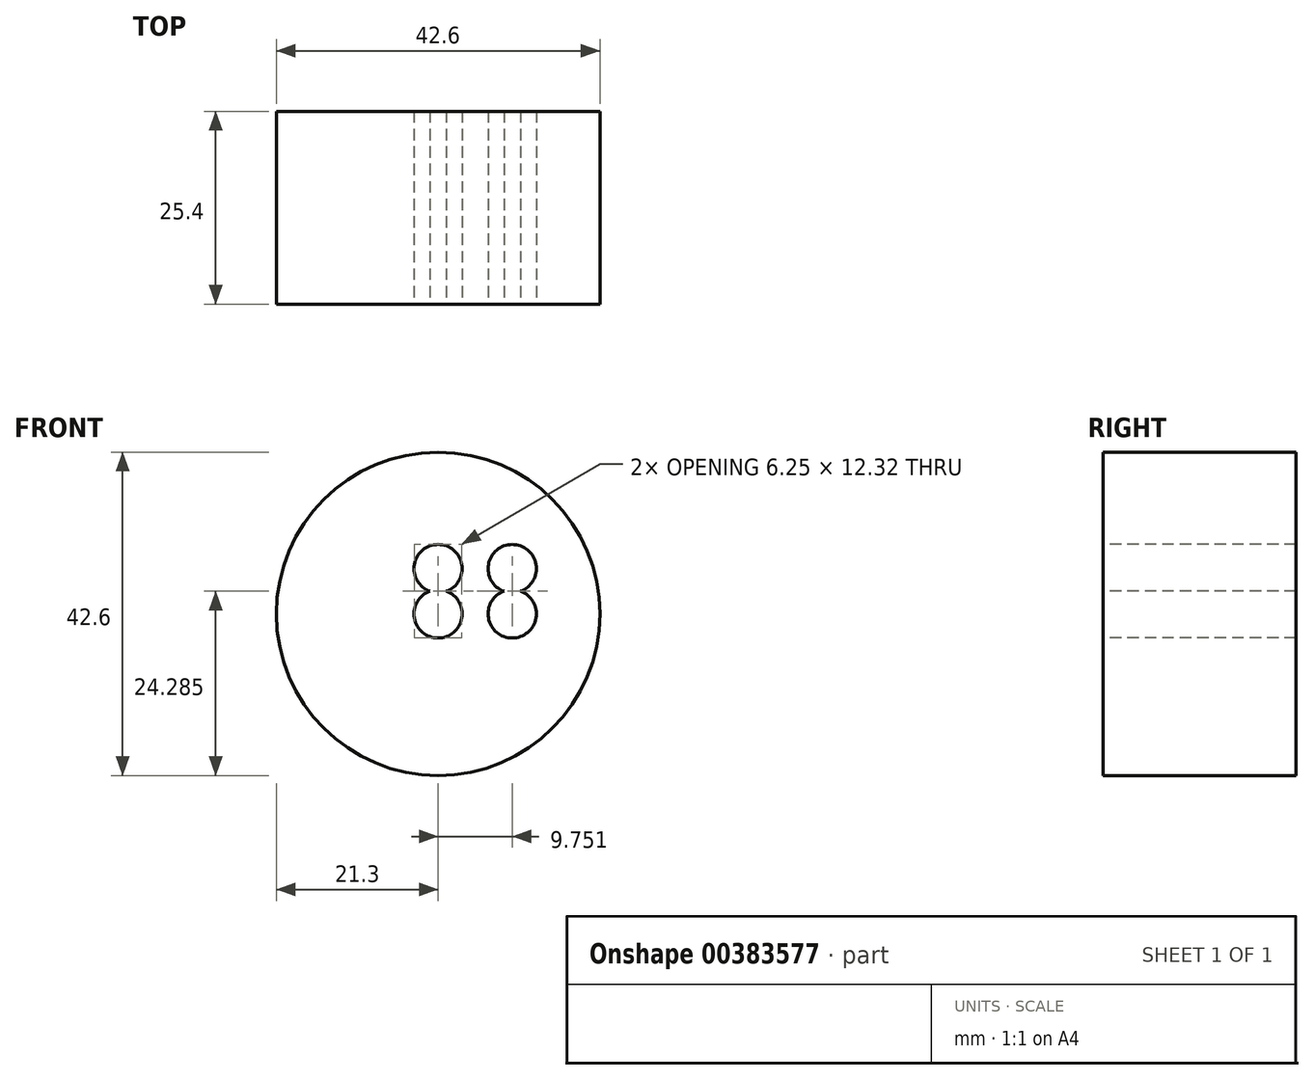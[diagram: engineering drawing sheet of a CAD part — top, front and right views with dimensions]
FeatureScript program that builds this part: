
annotation { "Feature Type Name" : "Feature", "Feature Type Description" : "" }
export const myFeature = defineFeature(function(context is Context, id is Id, definition is map)
    precondition{}
    {
        {
            var Q0;
            Q0=qCreatedBy(makeId("Front.planeOp"),FACE);
            var sketch = newSketch(context, id + "F0", { "sketchPlane" : qUnion([Q0])});
            skCircle(sketch, "E0", {"center": v(0, 0) * mm, "radius": 21.3 * mm});
            skSolve(sketch);
        }
        {
            var Q0;
            Q0 = qSketchRegion(id + "F0", true);
            extrude(context, id + "F1", {"entities" : qUnion([Q0]), "oppositeDirection" : true, "depth" : 25.4 * mm});
        }
        {
            var Q0;
            Q0=qCreatedBy(makeId("Front.planeOp"),FACE);
            var sketch = newSketch(context, id + "F2", { "sketchPlane" : qUnion([Q0])});
            skLineSegment(sketch, "E1.bottom", {"start": v(0, 0) * mm, "end": v(9.75, 0) * mm});
            skLineSegment(sketch, "E1.top", {"start": v(0, 5.97) * mm, "end": v(9.75, 5.97) * mm});
            skLineSegment(sketch, "E1.left", {"start": v(0, 0) * mm, "end": v(0, 5.97) * mm});
            skLineSegment(sketch, "E1.right", {"start": v(9.75, 0) * mm, "end": v(9.75, 5.97) * mm});
            skSolve(sketch);
        }
        {
            var Q0;
            Q0=sQuery(id+"F2.wireOp",VERTEX,"E1.right.start");
            var Q1;
            Q1=sQuery(id+"F2.wireOp",VERTEX,"E1.top.end");
            var Q2;
            Q2=sQuery(id+"F2.wireOp",VERTEX,"E1.left.start");
            var Q3;
            Q3=sQuery(id+"F2.wireOp",VERTEX,"E1.left.end");
            var Q4;
            Q4=makeQuery(id+"F1.opExtrude","SWEPT_BODY",BODY,{"disambiguationData":[OSD([sQuery(id+"F0.wireOp",EDGE,"E0")])]});
            hole(context, id + "F3", {"style" : HoleStyle.SIMPLE, "endStyle" : HoleEndStyle.THROUGH, "holeDiameter" : 6.35 * mm, "isTappedThrough" : true, "tappedDepth" : 12.7 * mm, "tapClearance" : 3, "locations" : qUnion([Q0, Q1, Q2, Q3]), "scope" : qUnion([Q4])});
        }
    });
